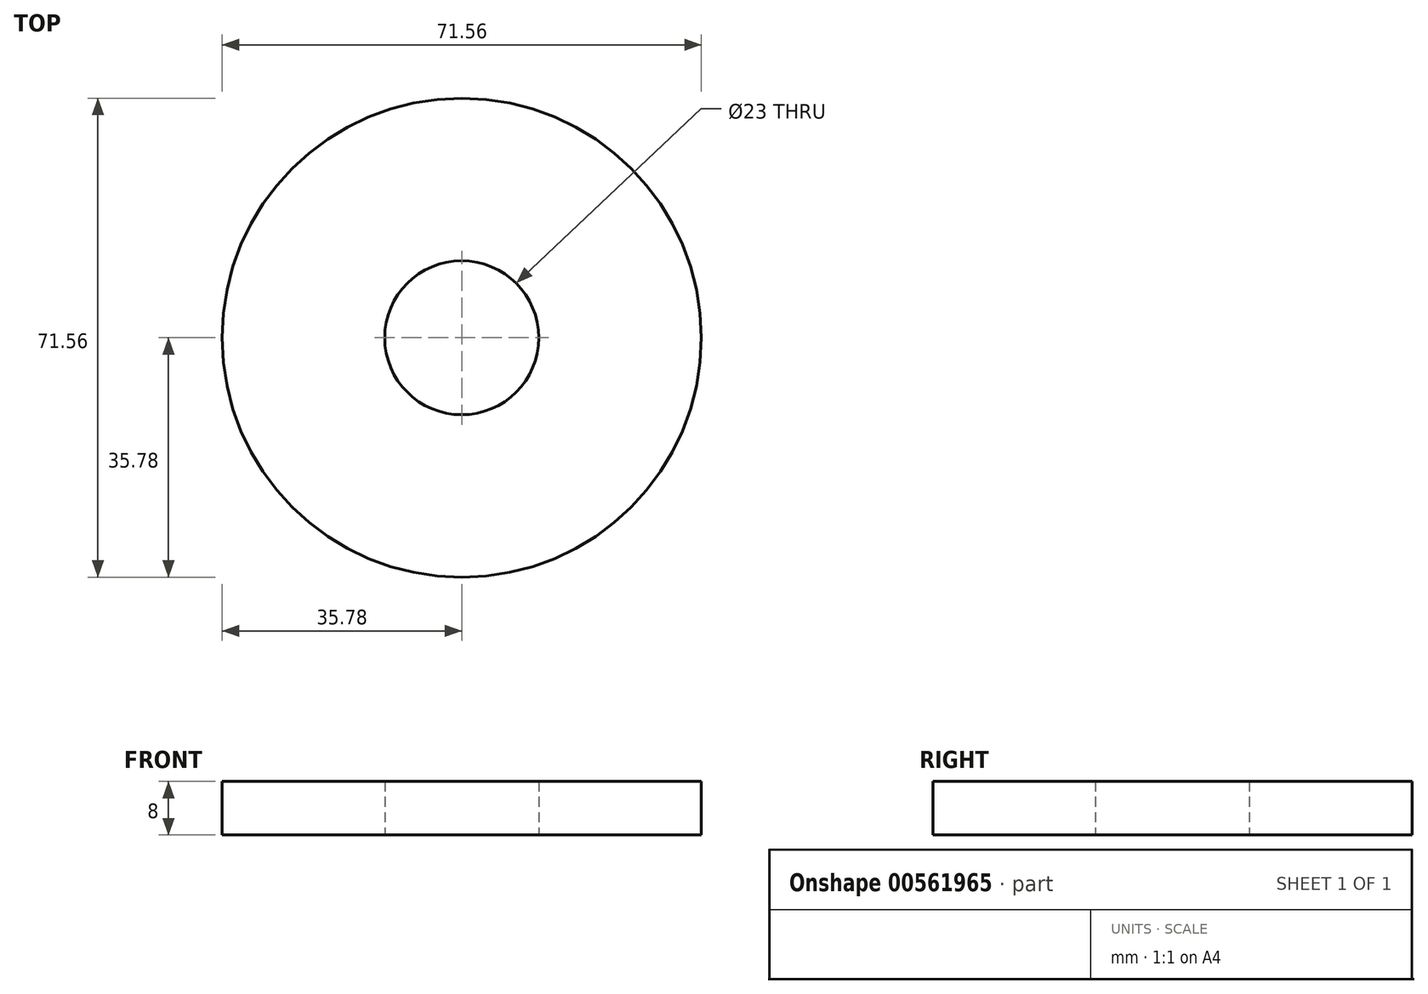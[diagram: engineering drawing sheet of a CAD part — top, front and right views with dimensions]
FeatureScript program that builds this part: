
annotation { "Feature Type Name" : "Feature", "Feature Type Description" : "" }
export const myFeature = defineFeature(function(context is Context, id is Id, definition is map)
    precondition{}
    {
        {
            var Q0;
            Q0=qCreatedBy(makeId("Top.planeOp"),FACE);
            var sketch = newSketch(context, id + "F0", { "sketchPlane" : qUnion([Q0])});
            skCircle(sketch, "E0", {"center": v(0, 0) * mm, "radius": 35.78 * mm});
            skCircle(sketch, "E1", {"center": v(0, 0) * mm, "radius": 11.5 * mm});
            skSolve(sketch);
        }
        {
            var Q0;
            Q0=makeQuery(id+"F0.imprint","IMPRINT",FACE,{"disambiguationData":[TD([[makeQuery(id+"F0.imprint","IMPRINT",EDGE,{"derivedFrom":sQuery(id+"F0.wireOp",EDGE,"E0")}),1.0]])]});
            extrude(context, id + "F1", {"entities" : qUnion([Q0]), "depth" : 8 * mm, "offsetDistance" : 25 * mm});
        }
    });
